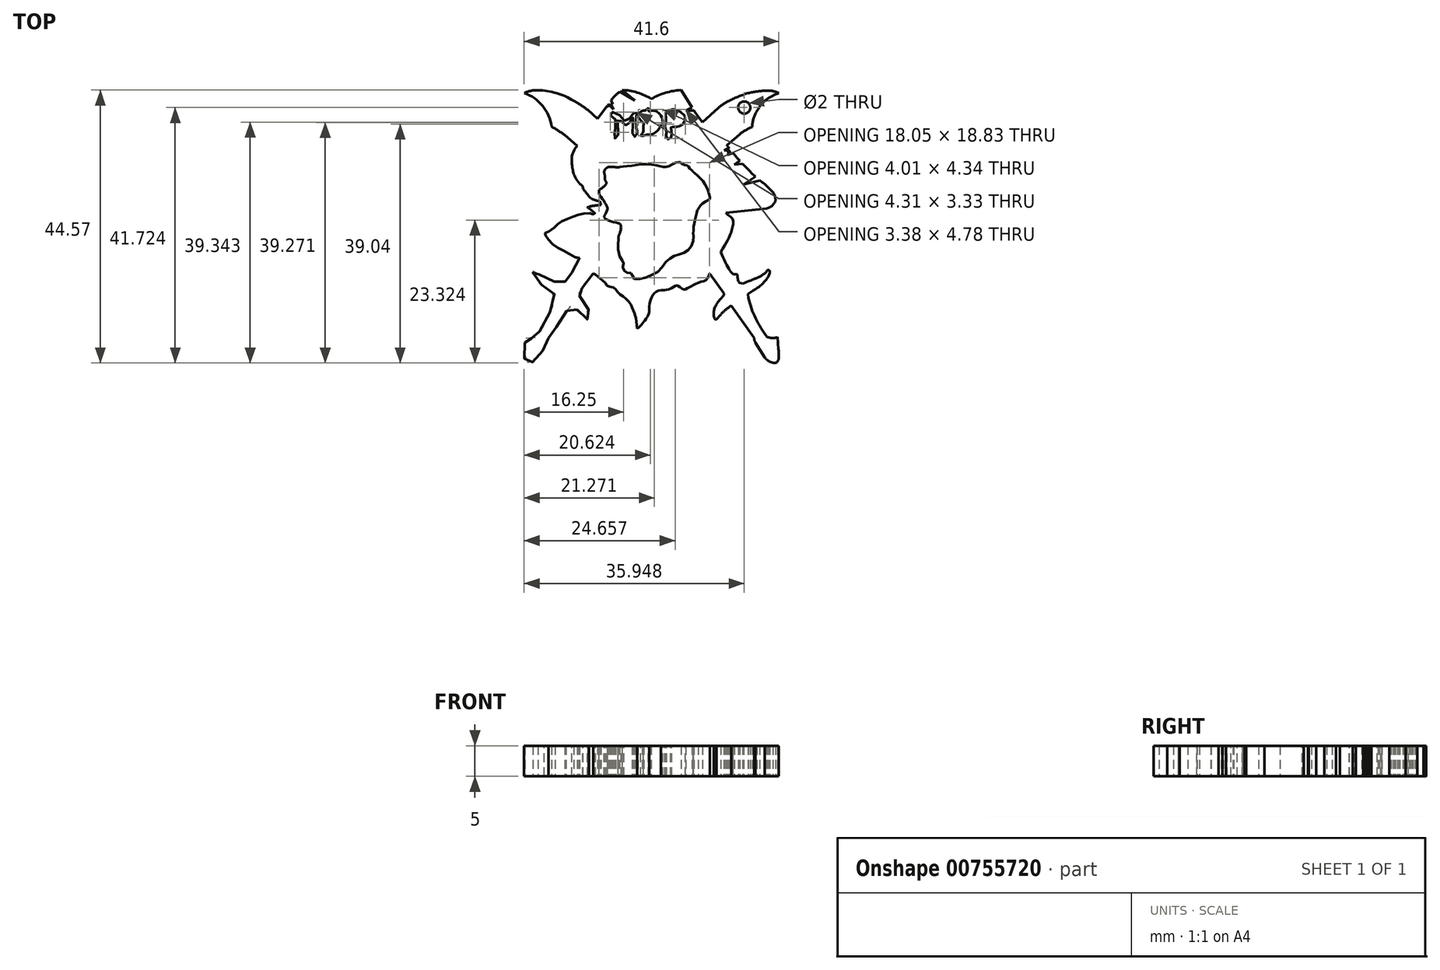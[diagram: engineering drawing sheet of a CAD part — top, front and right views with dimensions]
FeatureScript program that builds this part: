
annotation { "Feature Type Name" : "Feature", "Feature Type Description" : "" }
export const myFeature = defineFeature(function(context is Context, id is Id, definition is map)
    precondition{}
    {
        {
            var Q0;
            Q0=qCreatedBy(makeId("Top.planeOp"),FACE);
            var sketch = newSketch(context, id + "F0", { "sketchPlane" : qUnion([Q0])});
            skArc(sketch, "E0", {"start": v(-16.15, 15.64) * mm, "mid": v(-17.6, 19.02) * mm, "end": v(-20.6, 21.12) * mm});
            skArc(sketch, "E1", {"start": v(-18.37, 21.58) * mm, "mid": v(-19.52, 21.49) * mm, "end": v(-20.6, 21.12) * mm});
            skArc(sketch, "E2", {"start": v(-12.55, 19.88) * mm, "mid": v(-15.35, 21.1) * mm, "end": v(-18.37, 21.58) * mm});
            skArc(sketch, "E3", {"start": v(-10.26, 18.38) * mm, "mid": v(-11.38, 19.17) * mm, "end": v(-12.55, 19.88) * mm});
            skLineSegment(sketch, "E4", {"start": v(-10.26, 18.38) * mm, "end": v(-8.64, 16.93) * mm});
            skLineSegment(sketch, "E5", {"start": v(-8.64, 16.93) * mm, "end": v(-7.09, 19.04) * mm});
            skArc(sketch, "E6", {"start": v(-5, 21.35) * mm, "mid": v(-5.76, 20.7) * mm, "end": v(-6.42, 19.95) * mm});
            skArc(sketch, "E7", {"start": v(0.14, 20.17) * mm, "mid": v(-2.14, 21.21) * mm, "end": v(-4.62, 21.6) * mm});
            skArc(sketch, "E8", {"start": v(4.98, 21.6) * mm, "mid": v(2.47, 21.18) * mm, "end": v(0.14, 20.17) * mm});
            skLineSegment(sketch, "E9", {"start": v(4.98, 21.6) * mm, "end": v(6.81, 18.78) * mm});
            skLineSegment(sketch, "E10", {"start": v(7.82, 17.23) * mm, "end": v(8.51, 16.4) * mm});
            skLineSegment(sketch, "E11", {"start": v(8.51, 16.4) * mm, "end": v(11.1, 18.7) * mm});
            skArc(sketch, "E12", {"start": v(12.67, 19.78) * mm, "mid": v(11.85, 19.3) * mm, "end": v(11.1, 18.7) * mm});
            skArc(sketch, "E13", {"start": v(15.9, 21.1) * mm, "mid": v(14.26, 20.5) * mm, "end": v(12.67, 19.78) * mm});
            skArc(sketch, "E14", {"start": v(19.11, 21.53) * mm, "mid": v(17.5, 21.4) * mm, "end": v(15.9, 21.1) * mm});
            skArc(sketch, "E15", {"start": v(20.96, 21.1) * mm, "mid": v(20.06, 21.43) * mm, "end": v(19.11, 21.53) * mm});
            skArc(sketch, "E16", {"start": v(20.96, 21.1) * mm, "mid": v(19.97, 20.7) * mm, "end": v(19.06, 20.13) * mm});
            skArc(sketch, "E17", {"start": v(19.06, 20.13) * mm, "mid": v(18.12, 19.26) * mm, "end": v(17.4, 18.2) * mm});
            skArc(sketch, "E18", {"start": v(17.4, 18.2) * mm, "mid": v(16.82, 16.94) * mm, "end": v(16.63, 15.57) * mm});
            skArc(sketch, "E19", {"start": v(16.63, 15.57) * mm, "mid": v(15.51, 15.04) * mm, "end": v(14.5, 14.32) * mm});
            skLineSegment(sketch, "E20", {"start": v(14.5, 14.32) * mm, "end": v(12.48, 12.6) * mm});
            skArc(sketch, "E21", {"start": v(-14, 14.24) * mm, "mid": v(-15.05, 14.98) * mm, "end": v(-16.15, 15.64) * mm});
            skLineSegment(sketch, "E22", {"start": v(-14, 14.24) * mm, "end": v(-11.94, 12.46) * mm});
            skLineSegment(sketch, "E23", {"start": v(-5, 21.35) * mm, "end": v(-2.56, 19.94) * mm});
            skLineSegment(sketch, "E24", {"start": v(-2.56, 19.94) * mm, "end": v(-4.62, 21.6) * mm});
            skLineSegment(sketch, "E25", {"start": v(-6.42, 19.95) * mm, "end": v(-6.2, 19.28) * mm});
            skLineSegment(sketch, "E26", {"start": v(-6.2, 19.28) * mm, "end": v(-6.51, 19.4) * mm});
            skLineSegment(sketch, "E27", {"start": v(-6.51, 19.4) * mm, "end": v(-6.02, 18.44) * mm});
            skLineSegment(sketch, "E28", {"start": v(-6.02, 18.44) * mm, "end": v(-6.84, 19.38) * mm});
            skLineSegment(sketch, "E29", {"start": v(-6.84, 19.38) * mm, "end": v(-6.84, 18.86) * mm});
            skLineSegment(sketch, "E30", {"start": v(-6.84, 18.86) * mm, "end": v(-7.09, 19.04) * mm});
            skLineSegment(sketch, "E31", {"start": v(6.81, 18.78) * mm, "end": v(5.74, 18.3) * mm});
            skLineSegment(sketch, "E32", {"start": v(5.74, 18.3) * mm, "end": v(7.13, 18.3) * mm});
            skArc(sketch, "E33", {"start": v(12.48, 12.6) * mm, "mid": v(12.64, 12.39) * mm, "end": v(12.8, 12.18) * mm});
            skArc(sketch, "E34", {"start": v(20, 4.94) * mm, "mid": v(18.98, 5.96) * mm, "end": v(17.84, 6.85) * mm});
            skArc(sketch, "E35", {"start": v(20.4, 3.6) * mm, "mid": v(20.32, 4.3) * mm, "end": v(20, 4.94) * mm});
            skArc(sketch, "E36", {"start": v(19.3, 2.4) * mm, "mid": v(20, 2.87) * mm, "end": v(20.4, 3.6) * mm});
            skLineSegment(sketch, "E37", {"start": v(19.3, 2.4) * mm, "end": v(19, 2.26) * mm});
            skLineSegment(sketch, "E38", {"start": v(19, 2.26) * mm, "end": v(12.3, 1.55) * mm});
            skFitSpline(sketch, "E39", {"points": [v(12.3, 1.55) * mm, v(13.37, 0.6) * mm, v(13.4, -0.86) * mm, v(11.48, -4.84) * mm], "startDerivative": vector(4.9, -5.16) * mm, "endDerivative": vector(-8.45, -13.76) * mm});
            skFitSpline(sketch, "E40", {"points": [v(11.48, -4.84) * mm, v(13.6, -8.47) * mm, v(14.15, -8.52) * mm, v(14.53, -9.88) * mm], "startDerivative": vector(4.65, -10.28) * mm, "endDerivative": vector(4.24, -4.5) * mm});
            skLineSegment(sketch, "E41", {"start": v(14.53, -9.88) * mm, "end": v(15.08, -9.97) * mm});
            skFitSpline(sketch, "E42", {"points": [v(15.08, -9.97) * mm, v(17.55, -9) * mm, v(18.96, -8.08) * mm], "startDerivative": vector(7.94, 3.03) * mm, "endDerivative": vector(5.08, 3.9) * mm});
            skArc(sketch, "E43", {"start": v(19.5, -8.08) * mm, "mid": v(19.24, -7.8) * mm, "end": v(18.96, -8.08) * mm});
            skFitSpline(sketch, "E44", {"points": [v(19.5, -8.08) * mm, v(19.02, -9.2) * mm, v(17.96, -10.32) * mm, v(16.73, -11.16) * mm], "startDerivative": vector(-0.6, -4.14) * mm, "endDerivative": vector(-3.6, -2.19) * mm});
            skLineSegment(sketch, "E45", {"start": v(16.73, -11.16) * mm, "end": v(15.92, -11.73) * mm});
            skLineSegment(sketch, "E46", {"start": v(15.92, -11.73) * mm, "end": v(15.97, -12.35) * mm});
            skArc(sketch, "E47", {"start": v(15.97, -12.35) * mm, "mid": v(17.2, -15.7) * mm, "end": v(19.07, -18.72) * mm});
            skFitSpline(sketch, "E48", {"points": [v(19.07, -18.72) * mm, v(19.86, -18.9) * mm, v(20.77, -18.72) * mm], "startDerivative": vector(1.57, -0.49) * mm, "endDerivative": vector(2.46, 0.98) * mm});
            skLineSegment(sketch, "E49", {"start": v(20.77, -18.72) * mm, "end": v(20.9, -20.74) * mm});
            skFitSpline(sketch, "E50", {"points": [v(20.9, -20.74) * mm, v(20.9, -22.35) * mm, v(20.51, -22.9) * mm, v(20.1, -22.96) * mm, v(19.24, -22.6) * mm, v(18.66, -22.03) * mm], "startDerivative": vector(0.5, -2.92) * mm, "endDerivative": vector(-2.33, 2.8) * mm});
            skLineSegment(sketch, "E51", {"start": v(18.66, -22.03) * mm, "end": v(17.16, -19.67) * mm});
            skFitSpline(sketch, "E52", {"points": [v(17.16, -19.67) * mm, v(16.92, -18.85) * mm], "startDerivative": vector(-0.38, 0.66) * mm, "endDerivative": vector(-0.03, 1) * mm});
            skLineSegment(sketch, "E53", {"start": v(16.92, -18.85) * mm, "end": v(13.17, -13.6) * mm});
            skFitSpline(sketch, "E54", {"points": [v(13.17, -13.6) * mm, v(12, -14.52) * mm, v(10.81, -15.8) * mm], "startDerivative": vector(-2.48, -1.79) * mm, "endDerivative": vector(-2.23, -2.6) * mm});
            skFitSpline(sketch, "E55", {"points": [v(10.81, -15.8) * mm, v(10.6, -15.86) * mm, v(10.38, -15.48) * mm], "startDerivative": vector(-0.52, -0.3) * mm, "endDerivative": vector(-0.35, 0.87) * mm});
            skFitSpline(sketch, "E56", {"points": [v(10.38, -15.48) * mm, v(10.38, -14.36) * mm, v(11.07, -12.94) * mm, v(12.02, -11.9) * mm], "startDerivative": vector(-0.42, 3.6) * mm, "endDerivative": vector(2.89, 2.81) * mm});
            skLineSegment(sketch, "E57", {"start": v(12.02, -11.9) * mm, "end": v(12.02, -11.58) * mm});
            skLineSegment(sketch, "E58", {"start": v(12.02, -11.58) * mm, "end": v(9.7, -8.38) * mm});
            skFitSpline(sketch, "E59", {"points": [v(9.7, -8.38) * mm, v(9.37, -9.04) * mm, v(8.77, -9.58) * mm, v(7.85, -9.83) * mm, v(5.97, -10.8) * mm, v(5.55, -10.93) * mm, v(5.11, -10.8) * mm, v(4.58, -10.41) * mm, v(4.32, -10.3) * mm, v(4, -10.4) * mm, v(3.33, -10.81) * mm, v(2.57, -11.03) * mm, v(2.1, -11.06) * mm, v(1.68, -11.06) * mm], "startDerivative": vector(-3.25, -8.32) * mm, "endDerivative": vector(-6.8, 0.05) * mm});
            skFitSpline(sketch, "E60", {"points": [v(1.68, -11.06) * mm, v(1, -11.28) * mm, v(0.4, -11.83) * mm, v(0.06, -12.57) * mm, v(-0.13, -13.2) * mm, v(-0.2, -13.85) * mm, v(-0.22, -14.36) * mm, v(-0.23, -14.72) * mm, v(-0.39, -15.13) * mm, v(-0.58, -15.53) * mm, v(-0.88, -16) * mm, v(-1.14, -16.33) * mm, v(-1.45, -16.7) * mm, v(-1.76, -17) * mm, v(-2.17, -17.36) * mm], "startDerivative": vector(-8.43, -1.97) * mm, "endDerivative": vector(-6.01, -5.22) * mm});
            skFitSpline(sketch, "E61", {"points": [v(-2.17, -17.36) * mm, v(-2.28, -16.46) * mm, v(-2.4, -15.61) * mm, v(-2.5, -15.17) * mm, v(-2.72, -14.6) * mm, v(-2.99, -13.98) * mm, v(-3.32, -13.24) * mm, v(-4.03, -12.44) * mm, v(-4.82, -11.84) * mm, v(-5.47, -11.24) * mm, v(-5.94, -10.66) * mm, v(-6.92, -10.45) * mm, v(-7.29, -10.02) * mm, v(-7.81, -9.5) * mm, v(-8.39, -9.01) * mm, v(-8.98, -8.57) * mm, v(-9.31, -8.36) * mm], "startDerivative": vector(-1.78, 12.9) * mm, "endDerivative": vector(-6.94, 3.97) * mm});
            skFitSpline(sketch, "E62", {"points": [v(-11.59, -5.8) * mm, v(-12.36, -5.66) * mm, v(-13, -5.32) * mm, v(-13.7, -4.9) * mm, v(-14.68, -4.35) * mm, v(-15.18, -4.1) * mm, v(-15.76, -3.73) * mm, v(-16.4, -3.15) * mm, v(-16.78, -2.63) * mm, v(-17.09, -2.22) * mm, v(-17.24, -1.99) * mm, v(-17.32, -1.8) * mm, v(-17.15, -1.74) * mm, v(-16.97, -1.7) * mm, v(-16.39, -1.37) * mm, v(-15.64, -0.8) * mm, v(-15.25, -0.39) * mm, v(-15.08, -0.25) * mm, v(-14.74, 0) * mm, v(-14.2, 0.27) * mm, v(-13.6, 0.56) * mm, v(-12.85, 0.84) * mm, v(-12.15, 1.1) * mm, v(-11.59, 1.27) * mm, v(-11.01, 1.4) * mm, v(-10.36, 1.52) * mm, v(-9.63, 1.5) * mm, v(-9.43, 1.41) * mm, v(-9.27, 1.32) * mm, v(-8.99, 1.32) * mm, v(-9, 1.4) * mm, v(-9.15, 1.57) * mm, v(-9.58, 1.97) * mm, v(-10.23, 2.38) * mm, v(-10.29, 2.44) * mm, v(-10.29, 2.5) * mm, v(-10.24, 2.51) * mm, v(-10.18, 2.52) * mm, v(-9.88, 2.6) * mm, v(-9.38, 2.71) * mm, v(-8.71, 2.78) * mm, v(-8.04, 2.85) * mm, v(-7.7, 2.85) * mm, v(-7.57, 2.86) * mm, v(-7.48, 2.88) * mm, v(-7.5, 2.99) * mm, v(-7.8, 3.43) * mm, v(-7.9, 3.46) * mm, v(-8.26, 3.45) * mm, v(-8.88, 3.57) * mm, v(-9.42, 3.78) * mm, v(-9.96, 4.17) * mm, v(-10.14, 4.41) * mm, v(-10.52, 4.85) * mm, v(-10.75, 5.15) * mm, v(-11.02, 5.62) * mm, v(-11.02, 5.83) * mm, v(-11.4, 6.17) * mm, v(-12.2, 7.21) * mm, v(-12.51, 7.93) * mm, v(-12.7, 8.62) * mm, v(-12.81, 9.61) * mm, v(-12.83, 10.66) * mm, v(-12.75, 11.14) * mm, v(-12.2, 12.2) * mm, v(-11.94, 12.46) * mm], "startDerivative": vector(-39.69, 4.5) * mm, "endDerivative": vector(17.84, 12.4) * mm});
            skLineSegment(sketch, "E63", {"start": v(-12.36, -5.66) * mm, "end": v(-12.68, -4.33) * mm});
            skLineSegment(sketch, "E64", {"start": v(-12.68, -4.33) * mm, "end": v(-11.59, -5.8) * mm});
            skLineSegment(sketch, "E65", {"start": v(17.12, 7.5) * mm, "end": v(15.26, 6.2) * mm});
            skLineSegment(sketch, "E66", {"start": v(15.26, 6.2) * mm, "end": v(17.84, 6.85) * mm});
            skLineSegment(sketch, "E67", {"start": v(15.02, 9.6) * mm, "end": v(13.68, 9.45) * mm});
            skLineSegment(sketch, "E68", {"start": v(13.68, 9.45) * mm, "end": v(14.58, 10.07) * mm});
            skArc(sketch, "E69.trimOffspring", {"start": v(15.02, 9.6) * mm, "mid": v(16.05, 8.52) * mm, "end": v(17.12, 7.5) * mm});
            skLineSegment(sketch, "E70", {"start": v(12.8, 12.18) * mm, "end": v(12.08, 11.7) * mm});
            skLineSegment(sketch, "E71", {"start": v(12.08, 11.7) * mm, "end": v(12.87, 11.76) * mm});
            skLineSegment(sketch, "E72", {"start": v(12.87, 11.76) * mm, "end": v(12.49, 11.46) * mm});
            skLineSegment(sketch, "E73", {"start": v(12.49, 11.46) * mm, "end": v(13.06, 11.64) * mm});
            skLineSegment(sketch, "E74", {"start": v(13.06, 11.64) * mm, "end": v(12.58, 11.02) * mm});
            skLineSegment(sketch, "E75", {"start": v(12.58, 11.02) * mm, "end": v(13.5, 11.31) * mm});
            skArc(sketch, "E76.trimOffspring", {"start": v(13.5, 11.31) * mm, "mid": v(14.03, 10.69) * mm, "end": v(14.58, 10.07) * mm});
            skLineSegment(sketch, "E77.trimOffspring", {"start": v(7.13, 18.3) * mm, "end": v(7.82, 17.23) * mm});
            skFitSpline(sketch, "E78", {"points": [v(-11.59, -5.8) * mm, v(-12.1, -6.83) * mm, v(-12.62, -7.81) * mm, v(-13.2, -8.46) * mm, v(-13.87, -8.52) * mm, v(-13.82, -9) * mm, v(-14.13, -9.95) * mm, v(-14.42, -10) * mm, v(-14.62, -10) * mm, v(-14.8, -10) * mm, v(-16.22, -9.41) * mm, v(-16.84, -9.19) * mm, v(-17.75, -8.75) * mm, v(-18.62, -8.07) * mm, v(-18.7, -7.86) * mm, v(-18.97, -7.82) * mm, v(-19.2, -8.04) * mm, v(-19.03, -8.64) * mm, v(-18.57, -9.4) * mm, v(-17.91, -10.1) * mm, v(-16.97, -10.84) * mm, v(-16.05, -11.42) * mm, v(-15.66, -11.72) * mm, v(-15.63, -12.37) * mm, v(-16.2, -14.2) * mm, v(-17.15, -16.24) * mm, v(-18.05, -17.77) * mm, v(-18.46, -18.37) * mm, v(-18.7, -18.8) * mm, v(-19.03, -18.81) * mm, v(-19.64, -18.94) * mm, v(-20.4, -18.73) * mm, v(-20.5, -18.88) * mm, v(-20.5, -19.32) * mm, v(-20.56, -20.66) * mm, v(-20.61, -21.65) * mm, v(-20.61, -22.25) * mm, v(-20.47, -22.59) * mm, v(-20.17, -22.82) * mm, v(-19.73, -22.96) * mm, v(-19.26, -22.84) * mm, v(-18.72, -22.4) * mm, v(-18.1, -21.73) * mm, v(-17.36, -20.6) * mm, v(-16.78, -19.54) * mm, v(-16.63, -19.2) * mm, v(-16.64, -18.82) * mm, v(-16.33, -18.53) * mm, v(-16.17, -18.22) * mm, v(-15.5, -17.23) * mm, v(-14.48, -15.78) * mm, v(-13.8, -14.7) * mm, v(-13.13, -13.76) * mm, v(-12.9, -13.57) * mm, v(-12.22, -14.05) * mm, v(-11.29, -14.9) * mm, v(-10.55, -15.75) * mm, v(-10.47, -15.82) * mm, v(-10.3, -15.86) * mm, v(-10.2, -15.73) * mm, v(-10.1, -15.47) * mm, v(-10.06, -14.87) * mm, v(-10.08, -14.3) * mm, v(-10.5, -13.4) * mm, v(-11.06, -12.6) * mm, v(-11.72, -11.88) * mm, v(-11.73, -11.78) * mm, v(-11.69, -11.67) * mm, v(-11.7, -11.54) * mm, v(-11.47, -11.3) * mm, v(-11.07, -10.6) * mm, v(-10.34, -9.62) * mm, v(-9.31, -8.36) * mm], "startDerivative": vector(-28.65, -56.98) * mm, "endDerivative": vector(49.17, 60.35) * mm});
            skFitSpline(sketch, "E79", {"points": [v(-8.38, 5.31) * mm, v(-8.35, 4.64) * mm, v(-8.03, 4.07) * mm, v(-7.53, 3.38) * mm, v(-7.22, 2.8) * mm, v(-7, 2.32) * mm, v(-7.24, 1.56) * mm, v(-7.45, 1.14) * mm, v(-7.55, 0.79) * mm, v(-6.95, 0.37) * mm, v(-5.86, 0) * mm, v(-4.93, -0.3) * mm, v(-4.9, -1.43) * mm, v(-5.17, -2.17) * mm, v(-5.23, -2.73) * mm, v(-5.26, -4.56) * mm, v(-4.93, -5.8) * mm, v(-4.55, -6.28) * mm, v(-4.34, -6.52) * mm, v(-4.45, -6.95) * mm, v(-4.5, -7.33) * mm, v(-4.42, -7.72) * mm, v(-4.07, -8.06) * mm, v(-3.87, -8.2) * mm, v(-3.28, -8.19) * mm, v(-3.16, -8.35) * mm, v(-2.96, -8.69) * mm, v(-2.71, -9.03) * mm, v(-2.57, -9.24) * mm, v(-1.54, -9.22) * mm, v(-0.38, -8.87) * mm, v(0.7, -8.33) * mm, v(1.62, -7.71) * mm, v(2.43, -6.6) * mm, v(3, -6.07) * mm, v(3.48, -5.64) * mm, v(4.35, -5.32) * mm, v(5.08, -5.08) * mm, v(5.68, -4.86) * mm, v(6.27, -4.44) * mm, v(6.74, -3.79) * mm, v(7, -2.93) * mm, v(7, -2.27) * mm], "startDerivative": vector(-1.4, -30.07) * mm, "endDerivative": vector(-1.77, 27.28) * mm});
            skFitSpline(sketch, "E80", {"points": [v(7, -2.27) * mm, v(7, -1.32) * mm, v(7.17, 0) * mm, v(7.48, 1.2) * mm, v(7.57, 1.77) * mm, v(7.67, 1.96) * mm, v(8.07, 2.62) * mm, v(8.7, 3.23) * mm, v(9.7, 3.82) * mm, v(9.71, 3.86) * mm, v(9.7, 4.01) * mm, v(9.37, 5.2) * mm, v(8.8, 6.38) * mm, v(7.9, 7.45) * mm, v(6.68, 8.54) * mm, v(6.27, 9.04) * mm, v(6.1, 9.23) * mm, v(5.9, 9.32) * mm, v(5.36, 9.45) * mm, v(4.95, 9.75) * mm, v(4.77, 9.83) * mm, v(4.4, 9.8) * mm, v(3.73, 9.58) * mm, v(2.78, 9.1) * mm, v(2.19, 9.04) * mm, v(1.37, 9.23) * mm, v(0.82, 9.34) * mm, v(0.36, 9.43) * mm, v(-1.33, 9.5) * mm, v(-3.05, 9.28) * mm, v(-4.36, 9.14) * mm, v(-5.2, 9.02) * mm, v(-6.56, 9.07) * mm, v(-7.04, 8.97) * mm, v(-7.28, 8.78) * mm, v(-7.5, 8.52) * mm, v(-7.53, 7.97) * mm, v(-7.43, 7.53) * mm, v(-7.43, 7.16) * mm, v(-7.43, 6.99) * mm, v(-7.28, 6.72) * mm, v(-7.2, 6.47) * mm, v(-7.25, 6.24) * mm, v(-7.74, 5.74) * mm, v(-8.38, 5.31) * mm], "startDerivative": vector(-0.83, 32.9) * mm, "endDerivative": vector(-25.98, -15.62) * mm});
            skFitSpline(sketch, "E81", {"points": [v(-6.56, 9.07) * mm, v(-6.03, 8.8) * mm, v(-5.26, 8.2) * mm, v(-4.72, 7.7) * mm, v(-4.23, 7.27) * mm, v(-3.65, 6.87) * mm, v(-3.86, 6.67) * mm, v(-4.33, 6.37) * mm, v(-4.86, 6.32) * mm, v(-5.27, 6.48) * mm, v(-5.3, 6.9) * mm, v(-5.6, 7) * mm, v(-6.44, 7.24) * mm, v(-7.05, 7.46) * mm, v(-7.43, 7.53) * mm], "startDerivative": vector(6.84, -3.1) * mm, "endDerivative": vector(-6.12, 0.92) * mm});
            skFitSpline(sketch, "E82", {"points": [v(-7.43, 6.99) * mm, v(-7.09, 6.99) * mm, v(-6.7, 6.83) * mm, v(-6.56, 6.57) * mm, v(-6.4, 5.91) * mm, v(-6.56, 5.36) * mm, v(-6.83, 5.03) * mm, v(-7.07, 4.84) * mm, v(-7.21, 4.54) * mm, v(-7.13, 4.1) * mm, v(-6.7, 3.93) * mm, v(-6.25, 3.93) * mm, v(-5.83, 3.79) * mm, v(-5.53, 3.52) * mm, v(-5.35, 3.38) * mm, v(-5.12, 3.49) * mm, v(-4.74, 3.64) * mm, v(-4.47, 4.04) * mm, v(-4.44, 3.82) * mm, v(-4.42, 3.33) * mm, v(-4.57, 2.98) * mm, v(-4.8, 2.7) * mm, v(-4.97, 2.15) * mm, v(-5.13, 1.54) * mm, v(-4.93, 0.9) * mm, v(-4.84, 0.36) * mm, v(-4.44, 0) * mm, v(-4.44, 0.25) * mm, v(-4.33, 0.63) * mm, v(-4.2, 1.12) * mm, v(-4.04, 1.19) * mm, v(-3.77, 1.08) * mm, v(-3.8, 0.74) * mm, v(-3.68, 0.52) * mm, v(-3.42, 0.27) * mm, v(-3.06, 0.18) * mm, v(-2.79, 0.23) * mm, v(-2.65, 0.32) * mm, v(-2.35, 0.62) * mm, v(-1.77, 0.91) * mm, v(-1.58, 1) * mm, v(-1.5, 1.15) * mm, v(-1.55, 1.4) * mm, v(-2.2, 3.35) * mm, v(-2.87, 4.78) * mm, v(-3.43, 5.52) * mm, v(-3.73, 5.7) * mm, v(-4.04, 5.76) * mm, v(-4.28, 5.52) * mm, v(-4.4, 5.07) * mm, v(-4.47, 4.81) * mm, v(-4.51, 4.84) * mm, v(-4.59, 5.19) * mm, v(-4.61, 5.4) * mm, v(-4.59, 5.66) * mm, v(-4.37, 6) * mm, v(-4.04, 6.1) * mm, v(-3.72, 6.1) * mm, v(-3.64, 6.3) * mm, v(-3.56, 6.51) * mm, v(-3.32, 6.73) * mm, v(-2.75, 7.53) * mm, v(-3.27, 7.7) * mm, v(-4.32, 8.4) * mm, v(-4.86, 8.92) * mm, v(-4.96, 9.04) * mm], "startDerivative": vector(23.05, 2.15) * mm, "endDerivative": vector(-7.96, 11) * mm});
            skFitSpline(sketch, "E83", {"points": [v(-3.32, 6.73) * mm, v(-2.45, 6.32) * mm, v(-0.27, 5.44) * mm, v(-0.3, 5.2) * mm, v(-0.41, 4.34) * mm, v(-0.13, 3.3) * mm, v(0.62, 2.47) * mm, v(1.66, 2.03) * mm, v(3.4, 2.03) * mm, v(4.63, 2.5) * mm, v(5.22, 2.79) * mm, v(5.98, 3) * mm, v(6.4, 3.84) * mm, v(6.4, 5) * mm, v(6.03, 6.73) * mm, v(5.84, 7.05) * mm, v(6.24, 7.23) * mm, v(6.4, 7.4) * mm, v(6.82, 7.56) * mm, v(7.67, 7.66) * mm], "startDerivative": vector(11.56, -6.75) * mm, "endDerivative": vector(17.58, 1.26) * mm});
            skFitSpline(sketch, "E84", {"points": [v(6.82, 8.4) * mm, v(6.57, 8.22) * mm, v(5.27, 7.65) * mm, v(5.02, 7.64) * mm, v(4.42, 7.84) * mm, v(3.81, 8.08) * mm, v(3.13, 8.13) * mm, v(2.53, 7.87) * mm, v(2.17, 7.56) * mm, v(1.88, 7.21) * mm, v(1.3, 6.97) * mm, v(0.54, 6.9) * mm, v(-1.13, 7.13) * mm, v(-2.75, 7.53) * mm], "startDerivative": vector(-3.27, -2.98) * mm, "endDerivative": vector(-13.4, 3.73) * mm});
            skFitSpline(sketch, "E85", {"points": [v(-5.25, -3.06) * mm, v(-5.1, -3.25) * mm, v(-4.5, -3.06) * mm, v(-4.02, -3.1) * mm, v(-3.78, -3.17) * mm, v(-3.54, -3.08) * mm, v(-3.4, -3.17) * mm, v(-3.17, -3.28) * mm, v(-2.74, -3.28) * mm, v(-2.47, -2.96) * mm, v(-2.36, -3.02) * mm, v(-2.17, -3.27) * mm, v(-1.76, -3.34) * mm, v(-1.38, -3.21) * mm, v(-1.26, -3.3) * mm, v(-1.15, -3.44) * mm, v(-0.87, -3.5) * mm, v(-0.55, -3.4) * mm, v(-0.33, -3.11) * mm, v(-0.23, -3.23) * mm, v(0, -3.4) * mm, v(0.74, -3.03) * mm, v(0.8, -3.04) * mm, v(1.06, -3.05) * mm, v(1.47, -2.81) * mm, v(1.55, -2.87) * mm, v(1.68, -2.98) * mm, v(2, -2.98) * mm, v(2.46, -2.4) * mm, v(2.58, -1.95) * mm, v(2.58, -1.64) * mm, v(2.67, -1.63) * mm, v(2.77, -1.57) * mm, v(2.91, -1.33) * mm, v(2.98, -1.13) * mm, v(3.25, -0.7) * mm, v(3.62, -0.31) * mm, v(3.8, -0.4) * mm, v(4.11, -0.77) * mm, v(4.55, -1.68) * mm, v(4.6, -2.76) * mm, v(4.6, -3.3) * mm, v(4.23, -3.76) * mm, v(3.47, -4.34) * mm, v(2.8, -4.61) * mm, v(2.3, -4.9) * mm, v(2.28, -4.7) * mm, v(2.32, -4.37) * mm, v(2.25, -3.96) * mm, v(2.1, -3.97) * mm, v(1.5, -4.2) * mm, v(1.45, -4.37) * mm, v(1.39, -4.39) * mm, v(1.26, -4.38) * mm, v(0.86, -4.48) * mm, v(0.48, -4.76) * mm, v(0.44, -4.78) * mm, v(0.34, -4.78) * mm, v(-0.21, -4.95) * mm, v(-0.25, -4.96) * mm, v(-0.36, -4.8) * mm, v(-1.15, -4.87) * mm, v(-1.26, -4.85) * mm, v(-1.32, -4.72) * mm, v(-1.79, -4.7) * mm, v(-1.9, -4.8) * mm, v(-1.98, -4.85) * mm, v(-2.03, -4.85) * mm, v(-2.05, -4.67) * mm, v(-2.95, -4.6) * mm, v(-3.07, -4.7) * mm, v(-3.14, -4.76) * mm, v(-3.22, -4.66) * mm, v(-3.6, -4.48) * mm, v(-4.07, -4.56) * mm, v(-4.12, -4.53) * mm, v(-4.18, -4.43) * mm, v(-4.76, -4.45) * mm, v(-4.83, -4.4) * mm, v(-5, -4.35) * mm, v(-5.27, -4.43) * mm], "startDerivative": vector(9.93, -22.67) * mm, "endDerivative": vector(-22.52, -10) * mm});
            skFitSpline(sketch, "E86", {"points": [v(-6.53, 17.52) * mm, v(-5.84, 17.32) * mm, v(-5.73, 16.65) * mm, v(-5.66, 15.71) * mm, v(-5.84, 15.16) * mm, v(-5.86, 14.93) * mm, v(-5.83, 14.58) * mm, v(-6.02, 13.88) * mm, v(-5.94, 13.74) * mm, v(-5.48, 13.79) * mm, v(-5.23, 14.11) * mm, v(-5.27, 14.38) * mm, v(-5.36, 16.77) * mm, v(-5.3, 16.88) * mm, v(-5.12, 16.77) * mm, v(-4.72, 16.48) * mm, v(-4.25, 16.04) * mm, v(-4.02, 15.85) * mm, v(-3.9, 15.84) * mm, v(-3.72, 15.88) * mm, v(-3.57, 16.13) * mm, v(-3.35, 16.45) * mm, v(-3, 16.9) * mm, v(-2.76, 17.2) * mm, v(-2.83, 16.2) * mm, v(-2.83, 15.5) * mm, v(-2.98, 14.26) * mm, v(-3, 14.07) * mm, v(-2.65, 13.98) * mm, v(-2.38, 14.08) * mm, v(-2.07, 14.44) * mm, v(-2.14, 14.66) * mm, v(-2.22, 14.73) * mm, v(-2.28, 15.14) * mm, v(-2.34, 15.75) * mm, v(-2.4, 16.41) * mm, v(-2.33, 17.05) * mm, v(-2.25, 17.66) * mm, v(-2.22, 18.03) * mm, v(-2.42, 18.11) * mm, v(-2.64, 17.95) * mm, v(-3.13, 17.43) * mm, v(-3.44, 16.94) * mm, v(-3.74, 16.77) * mm, v(-4.14, 16.58) * mm, v(-4.38, 16.75) * mm, v(-4.78, 17.2) * mm, v(-5.28, 17.69) * mm, v(-5.92, 18) * mm, v(-6.48, 17.99) * mm, v(-6.63, 17.77) * mm, v(-6.53, 17.52) * mm]});
            skFitSpline(sketch, "E87", {"points": [v(-0.85, 18.28) * mm, v(-1.26, 18.23) * mm, v(-1.7, 17.97) * mm, v(-2, 17.7) * mm, v(-2, 17.23) * mm, v(-1.73, 16.81) * mm, v(-1.37, 16.44) * mm, v(-1.26, 16.55) * mm, v(-1.4, 16.85) * mm, v(-1.55, 17.25) * mm, v(-1.43, 17.65) * mm, v(-0.8, 17.88) * mm, v(-0.7, 17.77) * mm, v(-0.87, 17.48) * mm, v(-1, 17.18) * mm, v(-1.1, 16.08) * mm, v(-1.15, 15.41) * mm, v(-1.2, 14.73) * mm, v(-1.54, 14.29) * mm, v(-1.57, 14.16) * mm, v(-1.3, 14.13) * mm, v(-0.44, 14.33) * mm, v(0.2, 14.39) * mm, v(1.08, 14.93) * mm, v(1.42, 15.34) * mm, v(1.78, 15.88) * mm, v(1.93, 15.98) * mm, v(1.94, 16.96) * mm, v(1.33, 17.86) * mm, v(0.98, 18.12) * mm, v(0.47, 18.3) * mm, v(0, 18.2) * mm, v(-0.17, 18.15) * mm, v(-0.32, 18.25) * mm, v(-0.32, 18.62) * mm, v(-0.85, 18.28) * mm]});
            skFitSpline(sketch, "E88", {"points": [v(-0.41, 17.83) * mm, v(-0.47, 17.5) * mm, v(-0.47, 17.03) * mm, v(-0.64, 16.26) * mm, v(-0.45, 15.69) * mm, v(-0.41, 15.37) * mm, v(-0.48, 15) * mm, v(-0.27, 14.54) * mm, v(0, 14.68) * mm, v(0.28, 14.88) * mm, v(0.5, 15.09) * mm, v(0.83, 15.17) * mm, v(0.97, 15.34) * mm, v(1.13, 16.13) * mm, v(1.12, 16.88) * mm, v(0.84, 17.54) * mm, v(0.43, 17.9) * mm, v(-0.41, 17.83) * mm]});
            skLineSegment(sketch, "E89", {"start": v(-0.12, 17.93) * mm, "end": v(-0.17, 18.15) * mm});
            skLineSegment(sketch, "E90", {"start": v(0.1, 17.94) * mm, "end": v(0.1, 18.24) * mm});
            skLineSegment(sketch, "E91", {"start": v(-0.27, 14.54) * mm, "end": v(-0.27, 14.34) * mm});
            skLineSegment(sketch, "E92", {"start": v(0, 14.68) * mm, "end": v(0, 14.35) * mm});
            skLineSegment(sketch, "E93", {"start": v(-8.26, 3.45) * mm, "end": v(-8.04, 2.85) * mm});
            skLineSegment(sketch, "E94", {"start": v(-4.44, 0) * mm, "end": v(-4.93, -0.3) * mm});
            skLineSegment(sketch, "E95", {"start": v(-4.73, 0.2) * mm, "end": v(-5.2, -0.13) * mm});
            skPoint(sketch, "E96", {"position": v(15.32, 18.75) * mm});
            skLineSegment(sketch, "E97", {"start": v(-12.2, 7.21) * mm, "end": v(-11.87, 6.7) * mm});
            skLineSegment(sketch, "E98", {"start": v(-11.64, 6.42) * mm, "end": v(-11.4, 6.17) * mm});
            skLineSegment(sketch, "E99", {"start": v(-1.37, 16.44) * mm, "end": v(-1.1, 16.2) * mm});
            skLineSegment(sketch, "E100", {"start": v(-1.4, 16.85) * mm, "end": v(-1.06, 16.63) * mm});
            skPoint(sketch, "E101.3.internal.orphan", {"position": v(3.43, 17.93) * mm});
            skPoint(sketch, "E101.9.internal.orphan", {"position": v(3, 16.2) * mm});
            skPoint(sketch, "E102.11.internal.orphan", {"position": v(5.06, 15.98) * mm});
            skPoint(sketch, "E102.12.internal.orphan", {"position": v(5.36, 16.13) * mm});
            skPoint(sketch, "E102.4.internal.orphan", {"position": v(8, 16.2) * mm});
            skPoint(sketch, "E102.9.internal.orphan", {"position": v(4.2, 15.98) * mm});
            skPoint(sketch, "E103.22.internal.orphan", {"position": v(5.61, 15.98) * mm});
            skPoint(sketch, "E103.24.internal.orphan", {"position": v(6.21, 16.2) * mm});
            skPoint(sketch, "E103.4.internal.orphan", {"position": v(2.26, 16.2) * mm});
            skPoint(sketch, "E103.9.internal.orphan", {"position": v(3.08, 15.98) * mm});
            skPoint(sketch, "E104.end.orphan", {"position": v(3.43, 16.2) * mm});
            skPoint(sketch, "E105.start.orphan", {"position": v(3.43, 16.13) * mm});
            skPoint(sketch, "E106.start.orphan", {"position": v(6.42, 16.2) * mm});
            skFitSpline(sketch, "E107", {"points": [v(2.46, 17.73) * mm, v(2.55, 17.17) * mm, v(2.5, 16.2) * mm, v(2.37, 15.91) * mm, v(2.34, 15.64) * mm, v(2.45, 15.32) * mm, v(2.63, 14.62) * mm, v(2.55, 14.27) * mm, v(2.62, 14.08) * mm, v(2.8, 13.56) * mm, v(3.33, 13.86) * mm, v(3.5, 14.39) * mm, v(3.38, 14.94) * mm, v(3.37, 15.58) * mm, v(3.77, 15.6) * mm, v(4.47, 15.62) * mm, v(5.09, 15.87) * mm, v(5.72, 16.78) * mm, v(4.98, 18) * mm, v(3.19, 18.4) * mm, v(2.46, 17.73) * mm]});
            skFitSpline(sketch, "E108", {"points": [v(4.23, 17.48) * mm, v(3.57, 17.47) * mm, v(3.17, 17.53) * mm, v(3.1, 16.96) * mm, v(3.17, 16.4) * mm, v(4.4, 16.31) * mm, v(4.99, 16.93) * mm, v(4.23, 17.48) * mm]});
            skLineSegment(sketch, "E109", {"start": v(3.57, 17.47) * mm, "end": v(3.57, 18.46) * mm});
            skLineSegment(sketch, "E110", {"start": v(3.98, 17.49) * mm, "end": v(3.98, 18.42) * mm});
            skSolve(sketch);
        }
        {
            var Q0;
            Q0 = qSketchRegion(id + "F0", true);
            extrude(context, id + "F1", {"entities" : qUnion([Q0]), "depth" : 5 * mm, "offsetDistance" : 25 * mm});
        }
        {
            var Q0;
            Q0=sQuery(id+"F0.wireOp",VERTEX,"E96");
            var Q1;
            Q1=makeQuery(id+"F1.opExtrude","SWEPT_BODY",BODY,{"disambiguationData":[OSD([sQuery(id+"F0.wireOp",EDGE,"E0"),sQuery(id+"F0.wireOp",EDGE,"E1"),sQuery(id+"F0.wireOp",EDGE,"E2"),sQuery(id+"F0.wireOp",EDGE,"E3"),sQuery(id+"F0.wireOp",EDGE,"E4"),sQuery(id+"F0.wireOp",EDGE,"E5"),sQuery(id+"F0.wireOp",EDGE,"E6"),sQuery(id+"F0.wireOp",EDGE,"E7"),sQuery(id+"F0.wireOp",EDGE,"E8"),sQuery(id+"F0.wireOp",EDGE,"E9"),sQuery(id+"F0.wireOp",EDGE,"E10"),sQuery(id+"F0.wireOp",EDGE,"E11"),sQuery(id+"F0.wireOp",EDGE,"E12"),sQuery(id+"F0.wireOp",EDGE,"E13"),sQuery(id+"F0.wireOp",EDGE,"E14"),sQuery(id+"F0.wireOp",EDGE,"E15"),sQuery(id+"F0.wireOp",EDGE,"E16"),sQuery(id+"F0.wireOp",EDGE,"E17"),sQuery(id+"F0.wireOp",EDGE,"E18"),sQuery(id+"F0.wireOp",EDGE,"E19"),sQuery(id+"F0.wireOp",EDGE,"E20"),sQuery(id+"F0.wireOp",EDGE,"E21"),sQuery(id+"F0.wireOp",EDGE,"E22"),sQuery(id+"F0.wireOp",EDGE,"E23"),sQuery(id+"F0.wireOp",EDGE,"E24"),sQuery(id+"F0.wireOp",EDGE,"E25"),sQuery(id+"F0.wireOp",EDGE,"E26"),sQuery(id+"F0.wireOp",EDGE,"E27"),sQuery(id+"F0.wireOp",EDGE,"E28"),sQuery(id+"F0.wireOp",EDGE,"E29"),sQuery(id+"F0.wireOp",EDGE,"E30"),sQuery(id+"F0.wireOp",EDGE,"E31"),sQuery(id+"F0.wireOp",EDGE,"E32"),sQuery(id+"F0.wireOp",EDGE,"E33"),sQuery(id+"F0.wireOp",EDGE,"E34"),sQuery(id+"F0.wireOp",EDGE,"E35"),sQuery(id+"F0.wireOp",EDGE,"E36"),sQuery(id+"F0.wireOp",EDGE,"E37"),sQuery(id+"F0.wireOp",EDGE,"E38"),sQuery(id+"F0.wireOp",EDGE,"E39"),sQuery(id+"F0.wireOp",EDGE,"E40"),sQuery(id+"F0.wireOp",EDGE,"E41"),sQuery(id+"F0.wireOp",EDGE,"E42"),sQuery(id+"F0.wireOp",EDGE,"E43"),sQuery(id+"F0.wireOp",EDGE,"E44"),sQuery(id+"F0.wireOp",EDGE,"E45"),sQuery(id+"F0.wireOp",EDGE,"E46"),sQuery(id+"F0.wireOp",EDGE,"E47"),sQuery(id+"F0.wireOp",EDGE,"E48"),sQuery(id+"F0.wireOp",EDGE,"E49"),sQuery(id+"F0.wireOp",EDGE,"E50"),sQuery(id+"F0.wireOp",EDGE,"E51"),sQuery(id+"F0.wireOp",EDGE,"E52"),sQuery(id+"F0.wireOp",EDGE,"E53"),sQuery(id+"F0.wireOp",EDGE,"E54"),sQuery(id+"F0.wireOp",EDGE,"E55"),sQuery(id+"F0.wireOp",EDGE,"E56"),sQuery(id+"F0.wireOp",EDGE,"E57"),sQuery(id+"F0.wireOp",EDGE,"E58"),sQuery(id+"F0.wireOp",EDGE,"E59"),sQuery(id+"F0.wireOp",EDGE,"E60"),sQuery(id+"F0.wireOp",EDGE,"E61"),sQuery(id+"F0.wireOp",EDGE,"E62"),sQuery(id+"F0.wireOp",EDGE,"E63"),sQuery(id+"F0.wireOp",EDGE,"E64"),sQuery(id+"F0.wireOp",EDGE,"geS26LeR-lDkw-hcae-HQk2-HySWrc4lIqIB"),sQuery(id+"F0.wireOp",EDGE,"GrhGEohq-Q95n-m3vZ-Ztkw-16eyYqkvvZoa"),sQuery(id+"F0.wireOp",EDGE,"maXTR2Lw-gRRV-waak-3OAA-U0A50HmlAfab"),sQuery(id+"F0.wireOp",EDGE,"rPbKlpKq-kEUk-brZV-WeSc-S0V5wcrW1XgJ"),sQuery(id+"F0.wireOp",EDGE,"wHLPQnUs-ZVd1-J5Ci-6oUk-AgwUFcuaimR8"),sQuery(id+"F0.wireOp",EDGE,"sCsEfGIG-f91t-FLqj-mlHP-nrq9JrZlQ0TW"),sQuery(id+"F0.wireOp",EDGE,"E62"),sQuery(id+"F0.wireOp",EDGE,"E62"),sQuery(id+"F0.wireOp",EDGE,"E65"),sQuery(id+"F0.wireOp",EDGE,"E66"),sQuery(id+"F0.wireOp",EDGE,"E67"),sQuery(id+"F0.wireOp",EDGE,"E68"),sQuery(id+"F0.wireOp",EDGE,"E69.trimOffspring"),sQuery(id+"F0.wireOp",EDGE,"E70"),sQuery(id+"F0.wireOp",EDGE,"E71"),sQuery(id+"F0.wireOp",EDGE,"E72"),sQuery(id+"F0.wireOp",EDGE,"E73"),sQuery(id+"F0.wireOp",EDGE,"E74"),sQuery(id+"F0.wireOp",EDGE,"E75"),sQuery(id+"F0.wireOp",EDGE,"E76.trimOffspring"),sQuery(id+"F0.wireOp",EDGE,"E77.trimOffspring"),sQuery(id+"F0.wireOp",EDGE,"E78"),sQuery(id+"F0.wireOp",EDGE,"E79"),sQuery(id+"F0.wireOp",EDGE,"E80"),sQuery(id+"F0.wireOp",EDGE,"E81"),sQuery(id+"F0.wireOp",EDGE,"E82"),sQuery(id+"F0.wireOp",EDGE,"E83"),sQuery(id+"F0.wireOp",EDGE,"E84"),sQuery(id+"F0.wireOp",EDGE,"E82"),sQuery(id+"F0.wireOp",EDGE,"E85"),sQuery(id+"F0.wireOp",EDGE,"E86"),sQuery(id+"F0.wireOp",EDGE,"E87"),sQuery(id+"F0.wireOp",EDGE,"E88"),sQuery(id+"F0.wireOp",EDGE,"E103"),sQuery(id+"F0.wireOp",EDGE,"E101"),sQuery(id+"F0.wireOp",EDGE,"E102"),sQuery(id+"F0.wireOp",EDGE,"E80"),sQuery(id+"F0.wireOp",EDGE,"E80"),sQuery(id+"F0.wireOp",EDGE,"E79"),sQuery(id+"F0.wireOp",EDGE,"Zake5tuf-DzBc-DLnx-1Izn-0gsh1HGi4lmH"),sQuery(id+"F0.wireOp",EDGE,"QlDX0uhL-ALod-cLbe-YVbd-cGDRIcMdQSQ1"),sQuery(id+"F0.wireOp",EDGE,"4vT85MPm-MgPL-daYl-eWUE-XPcy8e4jBDpI"),sQuery(id+"F0.wireOp",EDGE,"4yUUWn9a-NZfz-0uyn-FQed-Bow53gWsDada"),sQuery(id+"F0.wireOp",EDGE,"eIUedkMx-ZYuI-CvcR-AYZ0-VRlpcAqZznTT"),sQuery(id+"F0.wireOp",EDGE,"5Y4ObPxt-B5k6-J7Qi-eujh-QftvNzi5RFdq"),sQuery(id+"F0.wireOp",EDGE,"E89"),sQuery(id+"F0.wireOp",EDGE,"E90"),sQuery(id+"F0.wireOp",EDGE,"E91"),sQuery(id+"F0.wireOp",EDGE,"E92"),sQuery(id+"F0.wireOp",EDGE,"E88"),sQuery(id+"F0.wireOp",EDGE,"E87"),sQuery(id+"F0.wireOp",EDGE,"b1b93dc8-d42b-4c02-9b09-9445c701f082.trimOffspring"),sQuery(id+"F0.wireOp",EDGE,"820c9efb-2be8-458a-bb7b-1666965391da.trimOffspring"),sQuery(id+"F0.wireOp",EDGE,"c5b3d09c-16a9-48a5-8c8c-9c5be07a1a07.trimOffspring"),sQuery(id+"F0.wireOp",EDGE,"E93"),sQuery(id+"F0.wireOp",EDGE,"E62"),sQuery(id+"F0.wireOp",EDGE,"E94"),sQuery(id+"F0.wireOp",EDGE,"E95"),sQuery(id+"F0.wireOp",EDGE,"E82"),sQuery(id+"F0.wireOp",EDGE,"E79")])]});
            hole(context, id + "F2", {"style" : HoleStyle.SIMPLE, "endStyle" : HoleEndStyle.BLIND, "oppositeDirection" : true, "standardTappedOrClearance" : lookupTablePath({ "standard" : "ISO", "size" : "2", "type" : "Drilled" }), "standardBlindInLast" : lookupTablePath({ "standard" : "ISO", "size" : "2", "type" : "Drilled" }), "holeDiameter" : 2 * mm, "majorDiameter" : 3 * mm, "holeDepth" : 13.5 * mm, "isTappedThrough" : true, "tappedDepth" : 12 * mm, "tapClearance" : 3, "locations" : qUnion([Q0]), "scope" : qUnion([Q1])});
        }
    });
